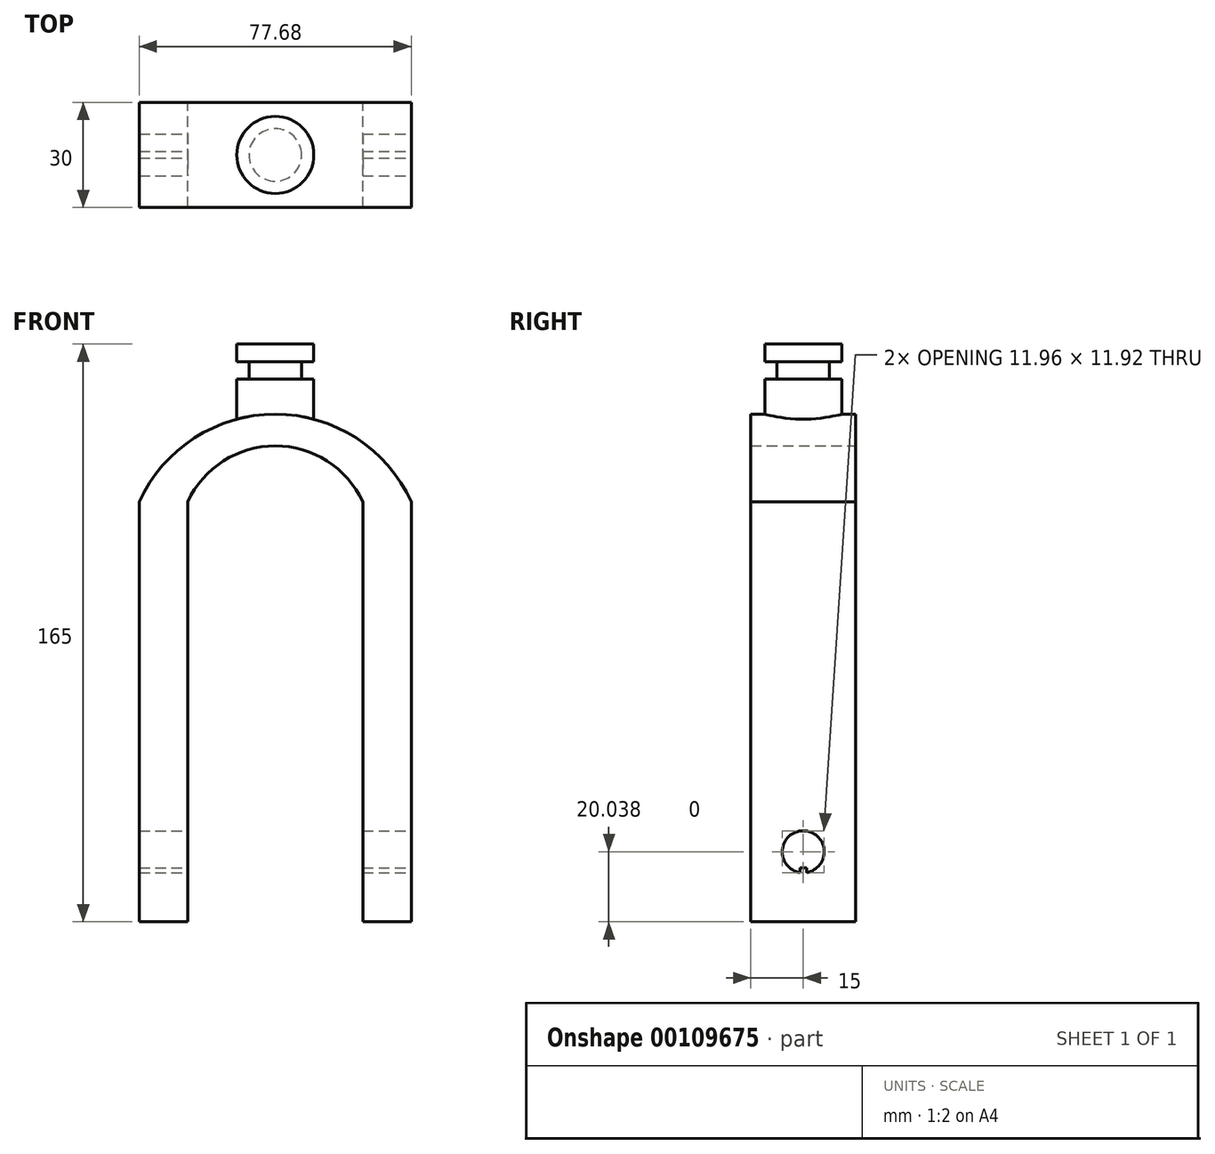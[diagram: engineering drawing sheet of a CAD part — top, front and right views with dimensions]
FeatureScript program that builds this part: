
annotation { "Feature Type Name" : "Feature", "Feature Type Description" : "" }
export const myFeature = defineFeature(function(context is Context, id is Id, definition is map)
    precondition{}
    {
        {
            var Q0;
            Q0=qCreatedBy(makeId("Front.planeOp"),FACE);
            var sketch = newSketch(context, id + "F0", { "sketchPlane" : qUnion([Q0])});
            skLineSegment(sketch, "E0.bottom", {"start": v(-38.84, 0) * mm, "end": v(-25, 0) * mm});
            skLineSegment(sketch, "E0.top", {"start": v(-38.84, 120) * mm, "end": v(-25, 120) * mm});
            skLineSegment(sketch, "E0.left", {"start": v(-38.84, 0) * mm, "end": v(-38.84, 120) * mm});
            skLineSegment(sketch, "E0.right", {"start": v(-25, 0) * mm, "end": v(-25, 120) * mm});
            skLineSegment(sketch, "E1.MirrorCS", {"start": v(25, 0) * mm, "end": v(25, 120) * mm});
            skLineSegment(sketch, "E2.MirrorCS", {"start": v(38.84, 120) * mm, "end": v(25, 120) * mm});
            skLineSegment(sketch, "E3.MirrorCS", {"start": v(38.84, 0) * mm, "end": v(38.84, 120) * mm});
            skLineSegment(sketch, "E4.MirrorCS", {"start": v(38.84, 0) * mm, "end": v(25, 0) * mm});
            skLineSegment(sketch, "E5", {"start": v(-25, 0) * mm, "end": v(25, 0) * mm, "construction": true});
            skArc(sketch, "E6", {"start": v(25, 120) * mm, "mid": v(0, 135.9) * mm, "end": v(-25, 120) * mm});
            skArc(sketch, "E7", {"start": v(38.84, 120) * mm, "mid": v(0, 144.97) * mm, "end": v(-38.84, 120) * mm});
            skSolve(sketch);
        }
        {
            var Q0;
            Q0=makeQuery(id+"F0.imprint","IMPRINT",FACE,{"disambiguationData":[TD([[makeQuery(id+"F0.imprint","IMPRINT",EDGE,{"derivedFrom":sQuery(id+"F0.wireOp",EDGE,"E0.top")}),1.0]])]});
            var Q1;
            Q1=makeQuery(id+"F0.imprint","IMPRINT",FACE,{"disambiguationData":[TD([[makeQuery(id+"F0.imprint","IMPRINT",EDGE,{"derivedFrom":sQuery(id+"F0.wireOp",EDGE,"E1.MirrorCS")}),-1.0]])]});
            var Q2;
            Q2=makeQuery(id+"F0.imprint","IMPRINT",FACE,{"disambiguationData":[TD([[makeQuery(id+"F0.imprint","IMPRINT",EDGE,{"derivedFrom":sQuery(id+"F0.wireOp",EDGE,"E0.bottom")}),1.0]])]});
            extrude(context, id + "F1", {"entities" : qUnion([Q0, Q1, Q2]), "depth" : 30 * mm});
        }
        {
            var Q0;
            Q0=makeQuery(id+"F1.opExtrude","SWEPT_FACE",FACE,{"disambiguationData":[OSD([sQuery(id+"F0.wireOp",EDGE,"E3.MirrorCS")])]});
            var sketch = newSketch(context, id + "F2", { "sketchPlane" : qUnion([Q0])});
            skLineSegment(sketch, "E8", {"start": v(-15, 0) * mm, "end": v(-15, 20) * mm, "construction": true});
            skCircle(sketch, "E9", {"center": v(-15, 20) * mm, "radius": 6 * mm});
            skLineSegment(sketch, "E10", {"start": v(-15.95, 14.08) * mm, "end": v(-14.05, 14.08) * mm});
            skLineSegment(sketch, "E11", {"start": v(-14.05, 14.08) * mm, "end": v(-14.05, 15.38) * mm});
            skLineSegment(sketch, "E12", {"start": v(-14.05, 15.38) * mm, "end": v(-15.95, 15.38) * mm});
            skLineSegment(sketch, "E13", {"start": v(-15.95, 15.38) * mm, "end": v(-15.95, 14.08) * mm});
            skSolve(sketch);
        }
        {
            var Q0;
            {var subQ3=sQuery(id+"F2.wireOp",EDGE,"E11");Q0=makeQuery(id+"F2.imprint","IMPRINT",FACE,{"disambiguationData":[TD([[makeQuery(id+"F2.imprint","IMPRINT",EDGE,{"derivedFrom":subQ3}),-1.0]])]});}
            var Q1;
            Q1=makeQuery(id+"F2.imprint","IMPRINT",FACE,{"disambiguationData":[TD([[makeQuery(id+"F2.imprint","IMPRINT",EDGE,{"derivedFrom":sQuery(id+"F2.wireOp",EDGE,"E10")}),1.0]])]});
            var Q2;
            {var subQ0=sQuery(id+"F2.wireOp",EDGE,"E10");Q2=makeQuery(id+"F2.imprint","IMPRINT",FACE,{"disambiguationData":[TD([[makeQuery(id+"F2.imprint","IMPRINT",EDGE,{"derivedFrom":subQ0}),-1.0]])]});}
            var Q3;
            Q3=makeQuery(id+"F1.opExtrude","SWEPT_FACE",FACE,{"disambiguationData":[OSD([sQuery(id+"F0.wireOp",EDGE,"E0.left")])]});
            extrude(context, id + "F3", {"entities" : qUnion([Q0, Q1, Q2]), "operationType" : NewBodyOperationType.REMOVE, "endBound" : BoundingType.UP_TO_SURFACE, "oppositeDirection" : true, "endBoundEntityFace" : qUnion([Q3]), "depth" : 25 * mm});
        }
        {
            var Q0;
            Q0=makeQuery(id+"F1.opExtrude","SWEPT_FACE",FACE,{"disambiguationData":[OSD([sQuery(id+"F0.wireOp",EDGE,"E3.MirrorCS")])]});
            var sketch = newSketch(context, id + "F4", { "sketchPlane" : qUnion([Q0])});
            skLineSegment(sketch, "E14", {"start": v(-15, 0) * mm, "end": v(-15, 20) * mm, "construction": true});
            skCircle(sketch, "E15", {"center": v(-15, 20) * mm, "radius": 2.5 * mm});
            skSolve(sketch);
        }
        {
            var Q0;
            Q0=makeQuery(id+"F2.imprint","IMPRINT",FACE,{"disambiguationData":[TD([[makeQuery(id+"F2.imprint","IMPRINT",EDGE,{"derivedFrom":sQuery(id+"F2.wireOp",EDGE,"E10")}),1.0]])]});
            var Q1;
            {var subQ0=sQuery(id+"F2.wireOp",EDGE,"E10");Q1=makeQuery(id+"F2.imprint","IMPRINT",FACE,{"disambiguationData":[TD([[makeQuery(id+"F2.imprint","IMPRINT",EDGE,{"derivedFrom":subQ0}),-1.0]])]});}
            var Q2;
            Q2=makeQuery(id+"F1.opExtrude","SWEPT_FACE",FACE,{"disambiguationData":[OSD([sQuery(id+"F0.wireOp",EDGE,"E1.MirrorCS")])]});
            extrude(context, id + "F5", {"entities" : qUnion([Q0, Q1]), "operationType" : NewBodyOperationType.ADD, "endBound" : BoundingType.UP_TO_SURFACE, "oppositeDirection" : true, "endBoundEntityFace" : qUnion([Q2]), "depth" : 25 * mm});
        }
        {
            var Q0;
            Q0=makeQuery(id+"F2.imprint","IMPRINT",FACE,{"disambiguationData":[TD([[makeQuery(id+"F2.imprint","IMPRINT",EDGE,{"derivedFrom":sQuery(id+"F2.wireOp",EDGE,"E10")}),1.0]])]});
            var Q1;
            {var subQ0=sQuery(id+"F2.wireOp",EDGE,"E10");Q1=makeQuery(id+"F2.imprint","IMPRINT",FACE,{"disambiguationData":[TD([[makeQuery(id+"F2.imprint","IMPRINT",EDGE,{"derivedFrom":subQ0}),-1.0]])]});}
            var Q2;
            Q2=makeQuery(id+"F1.opExtrude","SWEPT_FACE",FACE,{"disambiguationData":[OSD([sQuery(id+"F0.wireOp",EDGE,"E0.left")])]});
            var Q3;
            Q3=makeQuery(id+"F1.opExtrude","SWEPT_FACE",FACE,{"disambiguationData":[OSD([sQuery(id+"F0.wireOp",EDGE,"E0.right")])]});
            extrude(context, id + "F6", {"entities" : qUnion([Q0, Q1]), "operationType" : NewBodyOperationType.ADD, "endBound" : BoundingType.UP_TO_SURFACE, "oppositeDirection" : true, "endBoundEntityFace" : qUnion([Q2]), "depth" : 25 * mm, "hasSecondDirection" : true, "secondDirectionBound" : SecondDirectionBoundingType.UP_TO_SURFACE, "secondDirectionOppositeDirection" : true, "secondDirectionBoundEntityFace" : qUnion([Q3]), "secondDirectionDepth" : 25 * mm});
        }
        {
            var Q0;
            Q0=qCreatedBy(makeId("Top.planeOp"),FACE);
            var sketch = newSketch(context, id + "F7", { "sketchPlane" : qUnion([Q0])});
            skLineSegment(sketch, "E16.0.0", {"start": v(38.84, 0) * mm, "end": v(-38.84, 0) * mm});
            skLineSegment(sketch, "E16.0.1", {"start": v(-38.84, 0) * mm, "end": v(-38.84, -30) * mm});
            skLineSegment(sketch, "E16.0.2", {"start": v(-38.84, -30) * mm, "end": v(38.84, -30) * mm});
            skLineSegment(sketch, "E16.0.3", {"start": v(38.84, -30) * mm, "end": v(38.84, 0) * mm});
            skLineSegment(sketch, "E17", {"start": v(0, 0) * mm, "end": v(0, -30) * mm, "construction": true});
            skCircle(sketch, "E18", {"center": v(0, -15) * mm, "radius": 11 * mm});
            skCircle(sketch, "E19", {"center": v(0, -15) * mm, "radius": 7.5 * mm});
            skSolve(sketch);
        }
        {
            var Q0;
            Q0=makeQuery(id+"F7.imprint","IMPRINT",FACE,{"disambiguationData":[TD([[makeQuery(id+"F7.imprint","IMPRINT",EDGE,{"derivedFrom":sQuery(id+"F7.wireOp",EDGE,"E18")}),1.0]])]});
            var Q1;
            Q1=makeQuery(id+"F7.imprint","IMPRINT",FACE,{"disambiguationData":[TD([[makeQuery(id+"F7.imprint","IMPRINT",EDGE,{"derivedFrom":sQuery(id+"F7.wireOp",EDGE,"E19")}),1.0]])]});
            var Q2;
            Q2=makeQuery(id+"F1.opExtrude","SWEPT_FACE",FACE,{"disambiguationData":[OSD([sQuery(id+"F0.wireOp",EDGE,"E6")])]});
            var Q3;
            Q3=makeQuery(id+"F1.opExtrude","SWEPT_BODY",BODY,{"disambiguationData":[OSD([sQuery(id+"F0.wireOp",EDGE,"E0.bottom"),sQuery(id+"F0.wireOp",EDGE,"E0.left"),sQuery(id+"F0.wireOp",EDGE,"E0.right"),sQuery(id+"F0.wireOp",EDGE,"E1.MirrorCS"),sQuery(id+"F0.wireOp",EDGE,"E3.MirrorCS"),sQuery(id+"F0.wireOp",EDGE,"E4.MirrorCS"),sQuery(id+"F0.wireOp",EDGE,"E6"),sQuery(id+"F0.wireOp",EDGE,"E7")])]});
            extrude(context, id + "F8", {"entities" : qUnion([Q0, Q1]), "operationType" : NewBodyOperationType.ADD, "depth" : 165 * mm, "hasSecondDirection" : true, "secondDirectionBound" : SecondDirectionBoundingType.UP_TO_BODY, "secondDirectionOppositeDirection" : false, "secondDirectionBoundEntityFace" : qUnion([Q2]), "secondDirectionBoundEntityBody" : qUnion([Q3]), "secondDirectionDepth" : 138.64 * mm});
        }
        {
            var Q0;
            Q0=makeQuery(id+"F7.imprint","IMPRINT",FACE,{"disambiguationData":[TD([[makeQuery(id+"F7.imprint","IMPRINT",EDGE,{"derivedFrom":sQuery(id+"F7.wireOp",EDGE,"E18")}),1.0]])]});
            extrude(context, id + "F9", {"entities" : qUnion([Q0]), "operationType" : NewBodyOperationType.REMOVE, "depth" : 160 * mm, "hasSecondDirection" : true, "secondDirectionOppositeDirection" : false, "secondDirectionDepth" : 155 * mm});
        }
    });
